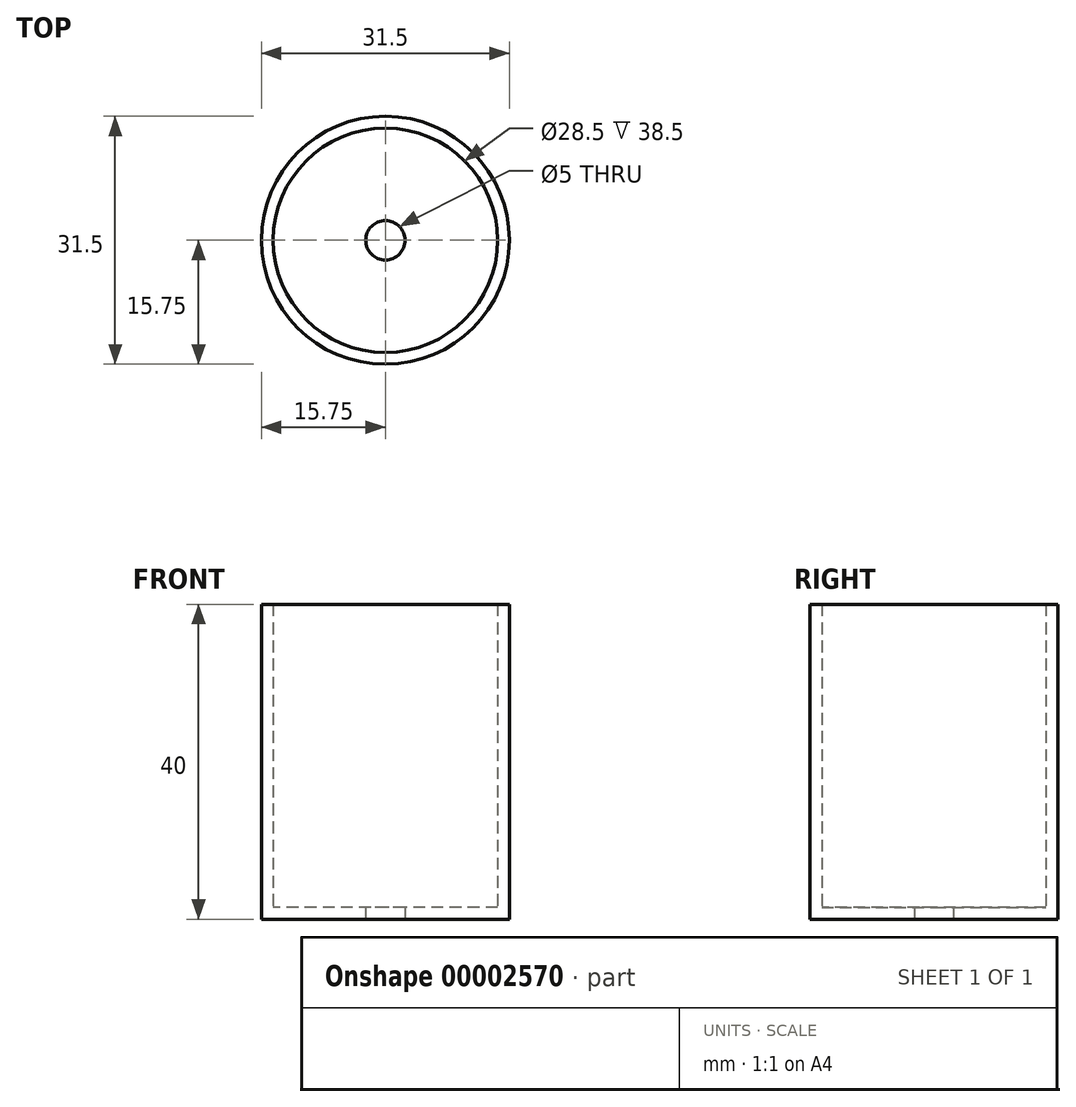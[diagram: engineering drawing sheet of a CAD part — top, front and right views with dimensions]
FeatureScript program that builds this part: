
annotation { "Feature Type Name" : "Feature", "Feature Type Description" : "" }
export const myFeature = defineFeature(function(context is Context, id is Id, definition is map)
    precondition{}
    {
        {
            var Q0;
            Q0=qCreatedBy(makeId("Top.planeOp"),FACE);
            var sketch = newSketch(context, id + "F0", { "sketchPlane" : qUnion([Q0])});
            skCircle(sketch, "E0", {"center": v(0, 0) * mm, "radius": 14.25 * mm});
            skCircle(sketch, "E1", {"center": v(0, 0) * mm, "radius": 15.75 * mm});
            skSolve(sketch);
        }
        {
            var Q0;
            Q0 = qSketchRegion(id + "F0", true);
            extrude(context, id + "F1", {"entities" : qUnion([Q0]), "depth" : 40 * mm});
        }
        {
            var Q0;
            Q0=qCreatedBy(makeId("Top.planeOp"),FACE);
            var sketch = newSketch(context, id + "F2", { "sketchPlane" : qUnion([Q0])});
            skCircle(sketch, "E2", {"center": v(0, 0) * mm, "radius": 14.25 * mm});
            skSolve(sketch);
        }
        {
            var Q0;
            Q0 = qSketchRegion(id + "F2", true);
            extrude(context, id + "F3", {"entities" : qUnion([Q0]), "operationType" : NewBodyOperationType.ADD, "depth" : 1.5 * mm});
        }
        {
            var Q0;
            Q0=makeQuery(id+"F3.boolean.opBoolean","MERGE",FACE,{"derivedFrom":[makeQuery(id+"F1.opExtrude","CAP_FACE",FACE,{"disambiguationData":[OSD([sQuery(id+"F0.wireOp",EDGE,"E0"),sQuery(id+"F0.wireOp",EDGE,"E1")])],"isStart":true}),makeQuery(id+"F3.opExtrude","CAP_FACE",FACE,{"disambiguationData":[OSD([sQuery(id+"F2.wireOp",EDGE,"E2")])],"isStart":true})]});
            var sketch = newSketch(context, id + "F4", { "sketchPlane" : qUnion([Q0])});
            skCircle(sketch, "E3", {"center": v(0, 0) * mm, "radius": 2.5 * mm});
            skSolve(sketch);
        }
        {
            var Q0;
            Q0 = qSketchRegion(id + "F4", true);
            extrude(context, id + "F5", {"entities" : qUnion([Q0]), "operationType" : NewBodyOperationType.REMOVE, "endBound" : BoundingType.UP_TO_NEXT, "oppositeDirection" : true, "depth" : 25 * mm});
        }
    });
